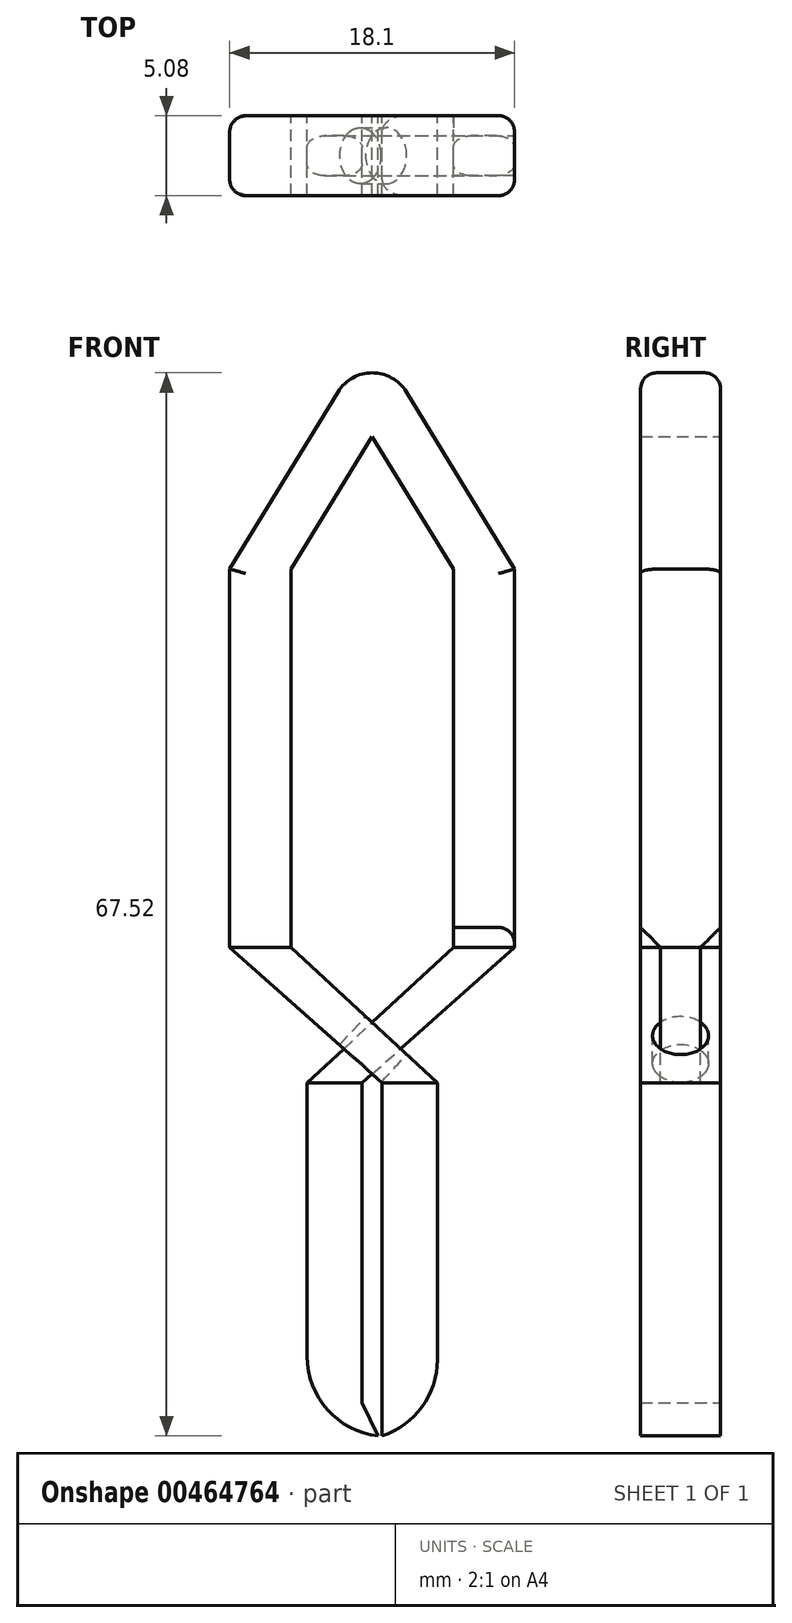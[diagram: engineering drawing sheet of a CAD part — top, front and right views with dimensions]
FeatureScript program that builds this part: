
annotation { "Feature Type Name" : "Feature", "Feature Type Description" : "" }
export const myFeature = defineFeature(function(context is Context, id is Id, definition is map)
    precondition{}
    {
        {
            var Q0;
            Q0=qCreatedBy(makeId("Front.planeOp"),FACE);
            var sketch = newSketch(context, id + "F0", { "sketchPlane" : qUnion([Q0])});
            skPoint(sketch, "E0", {"position": v(0, 30.17) * mm});
            skLineSegment(sketch, "E1", {"start": v(-5.15, 31.01) * mm, "end": v(-5.15, 6.98) * mm});
            skLineSegment(sketch, "E2", {"start": v(-9.05, 31.01) * mm, "end": v(-9.05, 6.98) * mm});
            skLineSegment(sketch, "E3", {"start": v(-9.05, 6.98) * mm, "end": v(-5.15, 6.98) * mm});
            skLineSegment(sketch, "E4", {"start": v(-5.15, 31.01) * mm, "end": v(-9.05, 31.01) * mm});
            skLineSegment(sketch, "E5.MirrorCS", {"start": v(5.15, 31.01) * mm, "end": v(5.15, 6.98) * mm});
            skLineSegment(sketch, "E6.MirrorCS", {"start": v(9.05, 31.01) * mm, "end": v(9.05, 6.98) * mm});
            skLineSegment(sketch, "E7.MirrorCS", {"start": v(5.15, 31.01) * mm, "end": v(9.05, 31.01) * mm});
            skLineSegment(sketch, "E8.MirrorCS", {"start": v(9.05, 6.98) * mm, "end": v(5.15, 6.98) * mm});
            skLineSegment(sketch, "E9", {"start": v(-9.05, 31.01) * mm, "end": v(0, 45.8) * mm});
            skLineSegment(sketch, "E10", {"start": v(0, 45.8) * mm, "end": v(9.05, 31.01) * mm});
            skLineSegment(sketch, "E11", {"start": v(5.15, 31.01) * mm, "end": v(0, 39.44) * mm});
            skLineSegment(sketch, "E12", {"start": v(0, 39.44) * mm, "end": v(-5.15, 31.01) * mm});
            skLineSegment(sketch, "E13", {"start": v(-0.64, -1.63) * mm, "end": v(-4.14, -1.63) * mm});
            skLineSegment(sketch, "E14", {"start": v(-4.14, -1.63) * mm, "end": v(-4.14, -24.04) * mm});
            skLineSegment(sketch, "E15", {"start": v(-4.14, -24.04) * mm, "end": v(-0.63, -24.04) * mm});
            skLineSegment(sketch, "E16", {"start": v(-0.63, -24.04) * mm, "end": v(-0.64, -1.63) * mm});
            skLineSegment(sketch, "E17.MirrorCS", {"start": v(0.64, -24.04) * mm, "end": v(0.64, -1.63) * mm});
            skLineSegment(sketch, "E18.MirrorCS", {"start": v(4.14, -1.63) * mm, "end": v(4.14, -24.04) * mm});
            skLineSegment(sketch, "E19.MirrorCS", {"start": v(0.64, -1.63) * mm, "end": v(4.14, -1.63) * mm});
            skLineSegment(sketch, "E20.MirrorCS", {"start": v(4.14, -24.04) * mm, "end": v(0.63, -24.04) * mm});
            skLineSegment(sketch, "E21", {"start": v(-9.05, 6.98) * mm, "end": v(0.64, -1.63) * mm});
            skLineSegment(sketch, "E22", {"start": v(-5.15, 6.98) * mm, "end": v(4.14, -1.63) * mm});
            skLineSegment(sketch, "E23", {"start": v(-4.14, -1.63) * mm, "end": v(5.15, 6.98) * mm});
            skLineSegment(sketch, "E24", {"start": v(-0.64, -1.63) * mm, "end": v(9.05, 6.98) * mm});
            skLineSegment(sketch, "E25", {"start": v(-0.63, -24.04) * mm, "end": v(0.38, -24.04) * mm});
            skLineSegment(sketch, "E26", {"start": v(0.38, -24.04) * mm, "end": v(-0.63, -21.93) * mm});
            skLineSegment(sketch, "E27", {"start": v(0.64, -21.93) * mm, "end": v(0.64, -24.04) * mm});
            skLineSegment(sketch, "E28", {"start": v(-0.38, -21.93) * mm, "end": v(0.63, -24.04) * mm});
            skLineSegment(sketch, "E29", {"start": v(-0.38, -21.93) * mm, "end": v(0.63, -21.93) * mm});
            skPoint(sketch, "E30", {"position": v(0, 2.2) * mm});
            skPoint(sketch, "E31", {"position": v(-1.8, 0.54) * mm});
            skPoint(sketch, "E32", {"position": v(1.8, 0.54) * mm});
            skPoint(sketch, "E33", {"position": v(0, -1.06) * mm});
            skPoint(sketch, "E34", {"position": v(0, 0.54) * mm});
            skPoint(sketch, "E35", {"position": v(0.9, 1.38) * mm});
            skPoint(sketch, "E36", {"position": v(-0.9, -0.26) * mm});
            skLineSegment(sketch, "E37", {"start": v(0.9, 1.38) * mm, "end": v(-0.9, -0.26) * mm});
            skPoint(sketch, "E38", {"position": v(7.06, 6.98) * mm});
            skPoint(sketch, "E39.endSnap0", {"position": v(-2.39, -1.63) * mm});
            skLineSegment(sketch, "E40", {"start": v(7.06, 6.98) * mm, "end": v(-3.67, -2.56) * mm});
            skSolve(sketch);
        }
        {
            var Q0;
            Q0=makeQuery(id+"F0.imprint","IMPRINT",FACE,{"disambiguationData":[TD([[makeQuery(id+"F0.imprint","IMPRINT",EDGE,{"derivedFrom":sQuery(id+"F0.wireOp",EDGE,"E4")}),-1.0]])]});
            var Q1;
            Q1=makeQuery(id+"F0.imprint","IMPRINT",FACE,{"disambiguationData":[TD([[makeQuery(id+"F0.imprint","IMPRINT",EDGE,{"derivedFrom":sQuery(id+"F0.wireOp",EDGE,"E5.MirrorCS")}),1.0]])]});
            var Q2;
            Q2=makeQuery(id+"F0.imprint","IMPRINT",FACE,{"disambiguationData":[TD([[makeQuery(id+"F0.imprint","IMPRINT",EDGE,{"derivedFrom":sQuery(id+"F0.wireOp",EDGE,"E1")}),-1.0]])]});
            var Q3;
            {var subQ3=sQuery(id+"F0.wireOp",EDGE,"E13");Q3=makeQuery(id+"F0.imprint","IMPRINT",FACE,{"disambiguationData":[TD([[makeQuery(id+"F0.imprint","IMPRINT",EDGE,{"derivedFrom":subQ3}),1.0]])]});}
            var Q4;
            Q4=makeQuery(id+"F0.imprint","IMPRINT",FACE,{"disambiguationData":[TD([[makeQuery(id+"F0.imprint","IMPRINT",EDGE,{"derivedFrom":sQuery(id+"F0.wireOp",EDGE,"E17.MirrorCS")}),-1.0]])]});
            var Q5;
            Q5=makeQuery(id+"F0.imprint","IMPRINT",FACE,{"disambiguationData":[TD([[makeQuery(id+"F0.imprint","IMPRINT",EDGE,{"derivedFrom":sQuery(id+"F0.wireOp",EDGE,"E27")}),-1.0]])]});
            var Q6;
            {var subQ0=sQuery(id+"F0.wireOp",EDGE,"E25");Q6=makeQuery(id+"F0.imprint","IMPRINT",FACE,{"disambiguationData":[TD([[makeQuery(id+"F0.imprint","IMPRINT",EDGE,{"derivedFrom":subQ0}),1.0]])]});}
            extrude(context, id + "F1", {"entities" : qUnion([Q0, Q1, Q2, Q3, Q4, Q5, Q6]), "depth" : 5.08 * mm, "symmetric" : true});
        }
        {
            var Q0;
            Q0=makeQuery(id+"F1.opExtrude","SWEPT_EDGE",EDGE,{"disambiguationData":[OSD([sQuery(id+"F0.wireOp",EDGE,"E9"),sQuery(id+"F0.wireOp",EDGE,"E10")])]});
            fillet(context, id + "F2", {"entities" : qUnion([Q0]), "radius" : 2.54 * mm, "tangentPropagation" : true, "allowEdgeOverflow" : false});
        }
        {
            var Q0;
            {var subQ0=sQuery(id+"F0.wireOp",EDGE,"E3");Q0=makeQuery(id+"F0.imprint","IMPRINT",FACE,{"disambiguationData":[TD([[makeQuery(id+"F0.imprint","IMPRINT",EDGE,{"derivedFrom":subQ0}),-1.0]])]});}
            var Q1;
            {var subQ0=sQuery(id+"F0.wireOp",EDGE,"E23");var subQ1=sQuery(id+"F0.wireOp",EDGE,"E21");var subQ2=makeQuery(id+"F0.imprint","INTERSECT",VERTEX,{"derivedFrom":[subQ1,subQ0]});Q1=makeQuery(id+"F0.imprint","IMPRINT",FACE,{"disambiguationData":[TD([[makeQuery(id+"F0.imprint","IMPRINT",EDGE,{"disambiguationData":[TD([[subQ2,-1.0]])],"derivedFrom":subQ1}),1.0]])]});}
            var Q2;
            {var subQ0=sQuery(id+"F0.wireOp",EDGE,"E19.MirrorCS");Q2=makeQuery(id+"F0.imprint","IMPRINT",FACE,{"disambiguationData":[TD([[makeQuery(id+"F0.imprint","IMPRINT",EDGE,{"derivedFrom":subQ0}),1.0]])]});}
            var Q3;
            {var subQ0=sQuery(id+"F0.wireOp",EDGE,"E37");Q3=makeQuery(id+"F0.imprint","IMPRINT",FACE,{"disambiguationData":[TD([[makeQuery(id+"F0.imprint","IMPRINT",EDGE,{"derivedFrom":subQ0}),1.0]])]});}
            var Q4;
            {var subQ0=sQuery(id+"F0.wireOp",EDGE,"E24");var subQ1=sQuery(id+"F0.wireOp",EDGE,"E21");var subQ2=makeQuery(id+"F0.imprint","INTERSECT",VERTEX,{"derivedFrom":[subQ1,subQ0]});Q4=makeQuery(id+"F0.imprint","IMPRINT",FACE,{"disambiguationData":[TD([[makeQuery(id+"F0.imprint","IMPRINT",EDGE,{"disambiguationData":[TD([[subQ2,1.0]])],"derivedFrom":subQ1}),1.0]])]});}
            var Q5;
            {var subQ0=sQuery(id+"F0.wireOp",EDGE,"E37");Q5=makeQuery(id+"F0.imprint","IMPRINT",FACE,{"disambiguationData":[TD([[makeQuery(id+"F0.imprint","IMPRINT",EDGE,{"derivedFrom":subQ0}),-1.0]])]});}
            extrude(context, id + "F3", {"entities" : qUnion([Q0, Q1, Q2, Q3, Q4, Q5]), "depth" : 5.08 * mm, "symmetric" : true});
        }
        {
            var Q0;
            Q0=makeQuery(id+"F3.opExtrude","SWEPT_FACE",FACE,{"disambiguationData":[OSD([sQuery(id+"F0.wireOp",EDGE,"E22")])]});
            var sketch = newSketch(context, id + "F4", { "sketchPlane" : qUnion([Q0])});
            skPoint(sketch, "E41", {"position": v(-0.28, 0) * mm});
            skSolve(sketch);
        }
        {
            var Q0;
            Q0=sQuery(id+"F4.wireOp",VERTEX,"E41");
            var Q1;
            Q1=makeQuery(id+"F3.opExtrude","SWEPT_BODY",BODY,{"disambiguationData":[OSD([sQuery(id+"F0.wireOp",EDGE,"E3"),sQuery(id+"F0.wireOp",EDGE,"E19.MirrorCS"),sQuery(id+"F0.wireOp",EDGE,"E21"),sQuery(id+"F0.wireOp",EDGE,"E22")])]});
            hole(context, id + "F5", {"style" : HoleStyle.SIMPLE, "endStyle" : HoleEndStyle.BLIND, "holeDiameter" : 3.56 * mm, "holeDepth" : 7.62 * mm, "isTappedThrough" : true, "tappedDepth" : 12.7 * mm, "tapClearance" : 3, "locations" : qUnion([Q0]), "scope" : qUnion([Q1])});
        }
        {
            var Q0;
            {var subQ3=sQuery(id+"F0.wireOp",EDGE,"E22");var subQ5=makeQuery(id+"F0.imprint","INTERSECT",VERTEX,{"derivedFrom":[subQ3,sQuery(id+"F0.wireOp",EDGE,"E37")]});Q0=makeQuery(id+"F0.imprint","IMPRINT",FACE,{"disambiguationData":[TD([[makeQuery(id+"F0.imprint","IMPRINT",EDGE,{"disambiguationData":[TD([[subQ5,1.0]])],"derivedFrom":subQ3}),1.0]])]});}
            var Q1;
            {var subQ0=sQuery(id+"F0.wireOp",EDGE,"E23");var subQ5=sQuery(id+"F0.wireOp",EDGE,"E22");var subQ6=makeQuery(id+"F0.imprint","INTERSECT",VERTEX,{"derivedFrom":[subQ5,subQ0]});Q1=makeQuery(id+"F0.imprint","IMPRINT",FACE,{"disambiguationData":[TD([[makeQuery(id+"F0.imprint","IMPRINT",EDGE,{"disambiguationData":[TD([[subQ6,-1.0]])],"derivedFrom":subQ5}),1.0]])]});}
            var Q2;
            {var subQ0=sQuery(id+"F0.wireOp",EDGE,"E23");var subQ1=sQuery(id+"F0.wireOp",EDGE,"E21");var subQ2=makeQuery(id+"F0.imprint","INTERSECT",VERTEX,{"derivedFrom":[subQ1,subQ0]});Q2=makeQuery(id+"F0.imprint","IMPRINT",FACE,{"disambiguationData":[TD([[makeQuery(id+"F0.imprint","IMPRINT",EDGE,{"disambiguationData":[TD([[subQ2,-1.0]])],"derivedFrom":subQ1}),1.0]])]});}
            var Q3;
            {var subQ0=sQuery(id+"F0.wireOp",EDGE,"E37");Q3=makeQuery(id+"F0.imprint","IMPRINT",FACE,{"disambiguationData":[TD([[makeQuery(id+"F0.imprint","IMPRINT",EDGE,{"derivedFrom":subQ0}),1.0]])]});}
            var Q4;
            {var subQ0=sQuery(id+"F0.wireOp",EDGE,"E23");var subQ5=sQuery(id+"F0.wireOp",EDGE,"E21");var subQ6=makeQuery(id+"F0.imprint","INTERSECT",VERTEX,{"derivedFrom":[subQ5,subQ0]});Q4=makeQuery(id+"F0.imprint","IMPRINT",FACE,{"disambiguationData":[TD([[makeQuery(id+"F0.imprint","IMPRINT",EDGE,{"disambiguationData":[TD([[subQ6,-1.0]])],"derivedFrom":subQ5}),-1.0]])]});}
            var Q5;
            {var subQ3=sQuery(id+"F0.wireOp",EDGE,"E21");var subQ5=makeQuery(id+"F0.imprint","INTERSECT",VERTEX,{"derivedFrom":[subQ3,sQuery(id+"F0.wireOp",EDGE,"E37")]});Q5=makeQuery(id+"F0.imprint","IMPRINT",FACE,{"disambiguationData":[TD([[makeQuery(id+"F0.imprint","IMPRINT",EDGE,{"disambiguationData":[TD([[subQ5,1.0]])],"derivedFrom":subQ3}),-1.0]])]});}
            var Q6;
            {var subQ0=sQuery(id+"F0.wireOp",EDGE,"E37");Q6=makeQuery(id+"F0.imprint","IMPRINT",FACE,{"disambiguationData":[TD([[makeQuery(id+"F0.imprint","IMPRINT",EDGE,{"derivedFrom":subQ0}),-1.0]])]});}
            extrude(context, id + "F6", {"entities" : qUnion([Q0, Q1, Q2, Q3, Q4, Q5, Q6]), "depth" : 2.54 * mm, "symmetric" : true});
        }
        {
            var Q0;
            Q0=makeQuery(id+"F6.opExtrude","CAP_EDGE",EDGE,{"disambiguationData":[OSD([sQuery(id+"F0.wireOp",EDGE,"E23")])],"isStart":false});
            var Q1;
            Q1=makeQuery(id+"F6.opExtrude","CAP_EDGE",EDGE,{"disambiguationData":[OSD([sQuery(id+"F0.wireOp",EDGE,"E24")])],"isStart":false});
            var Q2;
            Q2=makeQuery(id+"F6.opExtrude","CAP_EDGE",EDGE,{"disambiguationData":[OSD([sQuery(id+"F0.wireOp",EDGE,"E24")])],"isStart":true});
            var Q3;
            Q3=makeQuery(id+"F6.opExtrude","CAP_EDGE",EDGE,{"disambiguationData":[OSD([sQuery(id+"F0.wireOp",EDGE,"E23")])],"isStart":true});
            fillet(context, id + "F7", {"entities" : qUnion([Q0, Q1, Q2, Q3]), "radius" : 0.76 * mm, "tangentPropagation" : true, "allowEdgeOverflow" : false});
        }
        {
            var Q0;
            Q0=makeQuery(id+"F1.opExtrude","CAP_EDGE",EDGE,{"disambiguationData":[OSD([sQuery(id+"F0.wireOp",EDGE,"E8.MirrorCS")])],"isStart":true});
            var Q1;
            Q1=makeQuery(id+"F1.opExtrude","CAP_EDGE",EDGE,{"disambiguationData":[OSD([sQuery(id+"F0.wireOp",EDGE,"E8.MirrorCS")])],"isStart":false});
            chamfer(context, id + "F8", {"entities" : qUnion([Q0, Q1]), "width" : 1.27 * mm, "tangentPropagation" : true});
        }
        {
            var Q0;
            Q0=makeQuery(id+"F1.opExtrude","CAP_EDGE",EDGE,{"disambiguationData":[OSD([sQuery(id+"F0.wireOp",EDGE,"E2")])],"isStart":true});
            var Q1;
            Q1=makeQuery(id+"F1.opExtrude","CAP_EDGE",EDGE,{"disambiguationData":[OSD([sQuery(id+"F0.wireOp",EDGE,"E2")])],"isStart":false});
            var Q2;
            Q2=makeQuery(id+"F1.opExtrude","CAP_EDGE",EDGE,{"disambiguationData":[OSD([sQuery(id+"F0.wireOp",EDGE,"E6.MirrorCS")])],"isStart":false});
            var Q3;
            Q3=makeQuery(id+"F1.opExtrude","CAP_EDGE",EDGE,{"disambiguationData":[OSD([sQuery(id+"F0.wireOp",EDGE,"E6.MirrorCS")])],"isStart":true});
            var Q4;
            Q4=makeQuery(id+"F1.opExtrude","CAP_EDGE",EDGE,{"disambiguationData":[OSD([sQuery(id+"F0.wireOp",EDGE,"E10")])],"isStart":false});
            var Q5;
            {var subQ0=sQuery(id+"F0.wireOp",EDGE,"E10");var subQ1=sQuery(id+"F0.wireOp",EDGE,"E9");Q5=makeQuery(id+"F2.opFillet","BLEND_EDGE",EDGE,{"blendedFrom":[makeQuery(id+"F1.opExtrude","SWEPT_EDGE",EDGE,{"disambiguationData":[OSD([subQ1,subQ0])]}),makeQuery(id+"F1.opExtrude","CAP_FACE",FACE,{"disambiguationData":[OSD([sQuery(id+"F0.wireOp",EDGE,"E1"),sQuery(id+"F0.wireOp",EDGE,"E2"),sQuery(id+"F0.wireOp",EDGE,"E3"),sQuery(id+"F0.wireOp",EDGE,"E5.MirrorCS"),sQuery(id+"F0.wireOp",EDGE,"E6.MirrorCS"),sQuery(id+"F0.wireOp",EDGE,"E8.MirrorCS"),subQ1,subQ0,sQuery(id+"F0.wireOp",EDGE,"E11"),sQuery(id+"F0.wireOp",EDGE,"E12")])],"isStart":false})],"blendedInto":[makeQuery(id+"F1.opExtrude","CAP_FACE",FACE,{"disambiguationData":[OSD([sQuery(id+"F0.wireOp",EDGE,"E1"),sQuery(id+"F0.wireOp",EDGE,"E2"),sQuery(id+"F0.wireOp",EDGE,"E3"),sQuery(id+"F0.wireOp",EDGE,"E5.MirrorCS"),sQuery(id+"F0.wireOp",EDGE,"E6.MirrorCS"),sQuery(id+"F0.wireOp",EDGE,"E8.MirrorCS"),subQ1,subQ0,sQuery(id+"F0.wireOp",EDGE,"E11"),sQuery(id+"F0.wireOp",EDGE,"E12")])],"isStart":false})]});}
            var Q6;
            Q6=makeQuery(id+"F1.opExtrude","CAP_EDGE",EDGE,{"disambiguationData":[OSD([sQuery(id+"F0.wireOp",EDGE,"E10")])],"isStart":true});
            var Q7;
            {var subQ0=sQuery(id+"F0.wireOp",EDGE,"E10");var subQ1=sQuery(id+"F0.wireOp",EDGE,"E9");Q7=makeQuery(id+"F2.opFillet","BLEND_EDGE",EDGE,{"blendedFrom":[makeQuery(id+"F1.opExtrude","SWEPT_EDGE",EDGE,{"disambiguationData":[OSD([subQ1,subQ0])]}),makeQuery(id+"F1.opExtrude","CAP_FACE",FACE,{"disambiguationData":[OSD([sQuery(id+"F0.wireOp",EDGE,"E1"),sQuery(id+"F0.wireOp",EDGE,"E2"),sQuery(id+"F0.wireOp",EDGE,"E3"),sQuery(id+"F0.wireOp",EDGE,"E5.MirrorCS"),sQuery(id+"F0.wireOp",EDGE,"E6.MirrorCS"),sQuery(id+"F0.wireOp",EDGE,"E8.MirrorCS"),subQ1,subQ0,sQuery(id+"F0.wireOp",EDGE,"E11"),sQuery(id+"F0.wireOp",EDGE,"E12")])],"isStart":true})],"blendedInto":[makeQuery(id+"F1.opExtrude","CAP_FACE",FACE,{"disambiguationData":[OSD([sQuery(id+"F0.wireOp",EDGE,"E1"),sQuery(id+"F0.wireOp",EDGE,"E2"),sQuery(id+"F0.wireOp",EDGE,"E3"),sQuery(id+"F0.wireOp",EDGE,"E5.MirrorCS"),sQuery(id+"F0.wireOp",EDGE,"E6.MirrorCS"),sQuery(id+"F0.wireOp",EDGE,"E8.MirrorCS"),subQ1,subQ0,sQuery(id+"F0.wireOp",EDGE,"E11"),sQuery(id+"F0.wireOp",EDGE,"E12")])],"isStart":true})]});}
            var Q8;
            Q8=makeQuery(id+"F1.opExtrude","CAP_EDGE",EDGE,{"disambiguationData":[OSD([sQuery(id+"F0.wireOp",EDGE,"E9")])],"isStart":true});
            var Q9;
            Q9=makeQuery(id+"F1.opExtrude","CAP_EDGE",EDGE,{"disambiguationData":[OSD([sQuery(id+"F0.wireOp",EDGE,"E9")])],"isStart":false});
            var Q10;
            Q10=makeQuery(id+"F3.opExtrude","CAP_EDGE",EDGE,{"disambiguationData":[OSD([sQuery(id+"F0.wireOp",EDGE,"E21")])],"isStart":false});
            var Q11;
            Q11=makeQuery(id+"F3.opExtrude","CAP_EDGE",EDGE,{"disambiguationData":[OSD([sQuery(id+"F0.wireOp",EDGE,"E21")])],"isStart":true});
            fillet(context, id + "F9", {"entities" : qUnion([Q0, Q1, Q2, Q3, Q4, Q5, Q6, Q7, Q8, Q9, Q10, Q11]), "radius" : 1.02 * mm, "tangentPropagation" : true, "allowEdgeOverflow" : false});
        }
        {
            var Q0;
            Q0=makeQuery(id+"F1.opExtrude","SWEPT_EDGE",EDGE,{"disambiguationData":[OSD([sQuery(id+"F0.wireOp",EDGE,"E14"),sQuery(id+"F0.wireOp",EDGE,"E15")])]});
            var Q1;
            Q1=makeQuery(id+"F1.opExtrude","SWEPT_EDGE",EDGE,{"disambiguationData":[OSD([sQuery(id+"F0.wireOp",EDGE,"E18.MirrorCS"),sQuery(id+"F0.wireOp",EDGE,"E20.MirrorCS")])]});
            fillet(context, id + "F10", {"entities" : qUnion([Q0, Q1]), "radius" : 5.08 * mm, "tangentPropagation" : true, "allowEdgeOverflow" : false});
        }
    });
